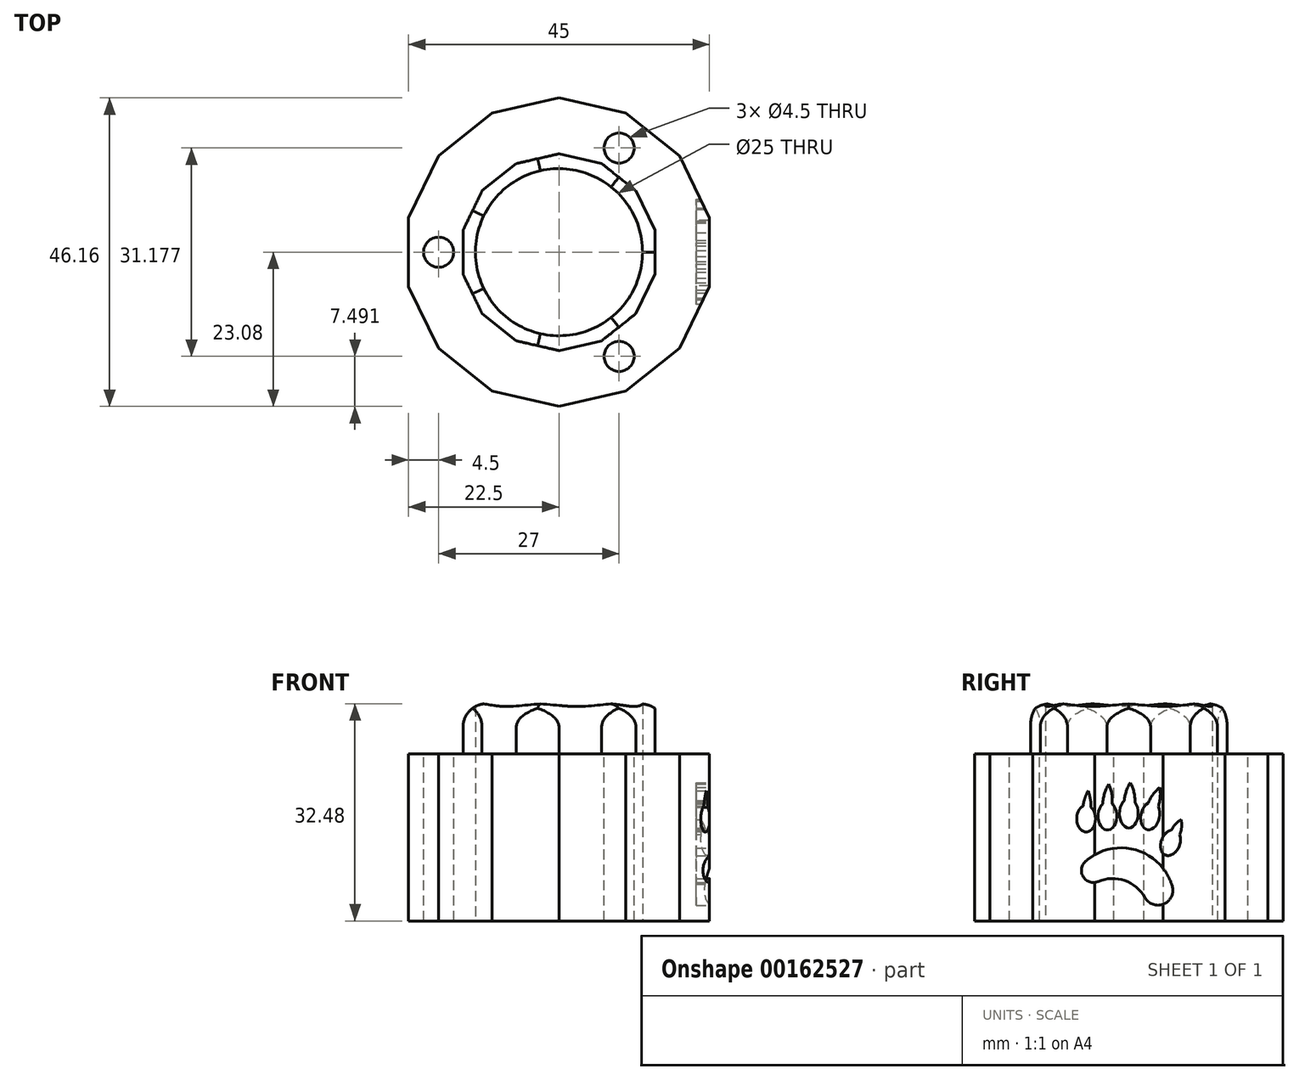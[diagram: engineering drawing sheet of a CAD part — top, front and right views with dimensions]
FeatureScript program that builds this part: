
annotation { "Feature Type Name" : "Feature", "Feature Type Description" : "" }
export const myFeature = defineFeature(function(context is Context, id is Id, definition is map)
    precondition{}
    {
        {
            var Q0;
            Q0=qCreatedBy(makeId("Top.planeOp"),FACE);
            var sketch = newSketch(context, id + "F0", { "sketchPlane" : qUnion([Q0])});
            skCircle(sketch, "E0", {"center": v(0, 0) * mm, "radius": 12.5 * mm});
            skCircle(sketch, "E1.cCircle", {"center": v(0, 0) * mm, "radius": 17.5 * mm, "construction": true});
            skLineSegment(sketch, "E1.0", {"start": v(17.5, 8.43) * mm, "end": v(17.5, -8.43) * mm, "construction": true});
            skLineSegment(sketch, "E1.1", {"start": v(17.5, -8.43) * mm, "end": v(4.32, -18.94) * mm, "construction": true});
            skLineSegment(sketch, "E1.2", {"start": v(4.32, -18.94) * mm, "end": v(-12.11, -15.19) * mm, "construction": true});
            skLineSegment(sketch, "E1.3", {"start": v(-12.11, -15.19) * mm, "end": v(-19.42, 0) * mm, "construction": true});
            skLineSegment(sketch, "E1.4", {"start": v(-19.42, 0) * mm, "end": v(-12.11, 15.19) * mm, "construction": true});
            skLineSegment(sketch, "E1.5", {"start": v(-12.11, 15.19) * mm, "end": v(4.32, 18.94) * mm, "construction": true});
            skLineSegment(sketch, "E1.6", {"start": v(4.32, 18.94) * mm, "end": v(17.5, 8.43) * mm, "construction": true});
            skPoint(sketch, "E1.0.midPoint", {"position": v(17.5, 0) * mm});
            skArc(sketch, "E2", {"start": v(7.16, 16.67) * mm, "mid": v(13.9, 17.43) * mm, "end": v(14.66, 10.69) * mm, "construction": true});
            skArc(sketch, "E3", {"start": v(0.79, 18.13) * mm, "mid": v(-4.96, 21.74) * mm, "end": v(-8.57, 16) * mm, "construction": true});
            skArc(sketch, "E4", {"start": v(-13.68, 11.92) * mm, "mid": v(-20.1, 9.68) * mm, "end": v(-17.85, 3.27) * mm, "construction": true});
            skArc(sketch, "E5", {"start": v(-17.85, -3.27) * mm, "mid": v(-20.1, -9.68) * mm, "end": v(-13.68, -11.92) * mm, "construction": true});
            skArc(sketch, "E6", {"start": v(-8.57, -16) * mm, "mid": v(-4.96, -21.74) * mm, "end": v(0.79, -18.13) * mm, "construction": true});
            skArc(sketch, "E7", {"start": v(14.66, -10.69) * mm, "mid": v(13.9, -17.43) * mm, "end": v(7.16, -16.67) * mm, "construction": true});
            skCircle(sketch, "E8.cCircle", {"center": v(0, 0) * mm, "radius": 22.5 * mm, "construction": true});
            skLineSegment(sketch, "E8.0", {"start": v(22.5, 5.14) * mm, "end": v(22.5, -5.14) * mm});
            skLineSegment(sketch, "E8.1", {"start": v(22.5, -5.14) * mm, "end": v(18.04, -14.39) * mm});
            skLineSegment(sketch, "E8.2", {"start": v(18.04, -14.39) * mm, "end": v(10.01, -20.8) * mm});
            skLineSegment(sketch, "E8.3", {"start": v(10.01, -20.8) * mm, "end": v(0, -23.08) * mm});
            skLineSegment(sketch, "E8.4", {"start": v(0, -23.08) * mm, "end": v(-10.01, -20.8) * mm});
            skLineSegment(sketch, "E8.5", {"start": v(-10.01, -20.8) * mm, "end": v(-18.04, -14.39) * mm});
            skLineSegment(sketch, "E8.6", {"start": v(-18.04, -14.39) * mm, "end": v(-22.5, -5.14) * mm});
            skLineSegment(sketch, "E8.7", {"start": v(-22.5, -5.14) * mm, "end": v(-22.5, 5.14) * mm});
            skLineSegment(sketch, "E8.8", {"start": v(-22.5, 5.14) * mm, "end": v(-18.04, 14.39) * mm});
            skLineSegment(sketch, "E8.9", {"start": v(-18.04, 14.39) * mm, "end": v(-10.01, 20.8) * mm});
            skLineSegment(sketch, "E8.10", {"start": v(-10.01, 20.8) * mm, "end": v(0, 23.08) * mm});
            skLineSegment(sketch, "E8.11", {"start": v(0, 23.08) * mm, "end": v(10.01, 20.8) * mm});
            skLineSegment(sketch, "E8.12", {"start": v(10.01, 20.8) * mm, "end": v(18.04, 14.39) * mm});
            skLineSegment(sketch, "E8.13", {"start": v(18.04, 14.39) * mm, "end": v(22.5, 5.14) * mm});
            skPoint(sketch, "E8.0.midPoint", {"position": v(22.5, 0) * mm});
            skSolve(sketch);
        }
        {
            var Q0;
            Q0=qSketchRegion(id+"F0",true);
            extrude(context, id + "F1", {"entities" : qUnion([Q0]), "endBound" : BoundingType.SYMMETRIC, "depth" : 25 * mm, "offsetDistance" : 25 * mm});
        }
        {
            var Q0;
            Q0=makeQuery(id+"F1.opExtrude","CAP_FACE",FACE,{"disambiguationData":[OSD([sQuery(id+"F0.wireOp",EDGE,"E0"),sQuery(id+"F0.wireOp",EDGE,"E1.0"),sQuery(id+"F0.wireOp",EDGE,"E1.1"),sQuery(id+"F0.wireOp",EDGE,"E1.2"),sQuery(id+"F0.wireOp",EDGE,"E1.3"),sQuery(id+"F0.wireOp",EDGE,"E1.4"),sQuery(id+"F0.wireOp",EDGE,"E1.5"),sQuery(id+"F0.wireOp",EDGE,"E1.6"),sQuery(id+"F0.wireOp",EDGE,"E2"),sQuery(id+"F0.wireOp",EDGE,"E3"),sQuery(id+"F0.wireOp",EDGE,"E4"),sQuery(id+"F0.wireOp",EDGE,"E5"),sQuery(id+"F0.wireOp",EDGE,"E6"),sQuery(id+"F0.wireOp",EDGE,"E7")])],"isStart":false});
            var sketch = newSketch(context, id + "F2", { "sketchPlane" : qUnion([Q0])});
            skLineSegment(sketch, "E9", {"start": v(0, 0) * mm, "end": v(11.38, 19.7) * mm, "construction": true});
            skCircle(sketch, "E10", {"center": v(9, 15.59) * mm, "radius": 2.25 * mm});
            skCircle(sketch, "E11.1.0", {"center": v(-18, 0) * mm, "radius": 2.25 * mm});
            skCircle(sketch, "E11.2.0", {"center": v(9, -15.59) * mm, "radius": 2.25 * mm});
            skPoint(sketch, "E11.center", {"position": v(0, 0) * mm});
            skSolve(sketch);
        }
        {
            var Q0;
            Q0=qSketchRegion(id+"F2",true);
            extrude(context, id + "F3", {"entities" : qUnion([Q0]), "operationType" : NewBodyOperationType.REMOVE, "oppositeDirection" : true, "depth" : 25 * mm, "offsetDistance" : 25 * mm});
        }
        {
            var Q0;
            Q0=makeQuery(id+"F1.opExtrude","CAP_FACE",FACE,{"disambiguationData":[OSD([sQuery(id+"F0.wireOp",EDGE,"E0"),sQuery(id+"F0.wireOp",EDGE,"E1.0"),sQuery(id+"F0.wireOp",EDGE,"E1.1"),sQuery(id+"F0.wireOp",EDGE,"E1.2"),sQuery(id+"F0.wireOp",EDGE,"E1.3"),sQuery(id+"F0.wireOp",EDGE,"E1.4"),sQuery(id+"F0.wireOp",EDGE,"E1.5"),sQuery(id+"F0.wireOp",EDGE,"E1.6"),sQuery(id+"F0.wireOp",EDGE,"E2"),sQuery(id+"F0.wireOp",EDGE,"E3"),sQuery(id+"F0.wireOp",EDGE,"E4"),sQuery(id+"F0.wireOp",EDGE,"E5"),sQuery(id+"F0.wireOp",EDGE,"E6"),sQuery(id+"F0.wireOp",EDGE,"E7")])],"isStart":false});
            var sketch = newSketch(context, id + "F4", { "sketchPlane" : qUnion([Q0])});
            skCircle(sketch, "E12", {"center": v(0, 0) * mm, "radius": 12.5 * mm});
            skCircle(sketch, "E13.cCircle", {"center": v(0, 0) * mm, "radius": 14.35 * mm, "construction": true});
            skLineSegment(sketch, "E13.0", {"start": v(14.35, 3.28) * mm, "end": v(14.35, -3.28) * mm});
            skLineSegment(sketch, "E13.1", {"start": v(14.35, -3.28) * mm, "end": v(11.5, -9.18) * mm});
            skLineSegment(sketch, "E13.2", {"start": v(11.5, -9.18) * mm, "end": v(6.39, -13.26) * mm});
            skLineSegment(sketch, "E13.3", {"start": v(6.39, -13.26) * mm, "end": v(0, -14.72) * mm});
            skLineSegment(sketch, "E13.4", {"start": v(0, -14.72) * mm, "end": v(-6.39, -13.26) * mm});
            skLineSegment(sketch, "E13.5", {"start": v(-6.39, -13.26) * mm, "end": v(-11.5, -9.18) * mm});
            skLineSegment(sketch, "E13.6", {"start": v(-11.5, -9.18) * mm, "end": v(-14.35, -3.28) * mm});
            skLineSegment(sketch, "E13.7", {"start": v(-14.35, -3.28) * mm, "end": v(-14.35, 3.28) * mm});
            skLineSegment(sketch, "E13.8", {"start": v(-14.35, 3.28) * mm, "end": v(-11.5, 9.18) * mm});
            skLineSegment(sketch, "E13.9", {"start": v(-11.5, 9.18) * mm, "end": v(-6.39, 13.26) * mm});
            skLineSegment(sketch, "E13.10", {"start": v(-6.39, 13.26) * mm, "end": v(0, 14.72) * mm});
            skLineSegment(sketch, "E13.11", {"start": v(0, 14.72) * mm, "end": v(6.39, 13.26) * mm});
            skLineSegment(sketch, "E13.12", {"start": v(6.39, 13.26) * mm, "end": v(11.5, 9.18) * mm});
            skLineSegment(sketch, "E13.13", {"start": v(11.5, 9.18) * mm, "end": v(14.35, 3.28) * mm});
            skPoint(sketch, "E13.0.midPoint", {"position": v(14.35, 0) * mm});
            skSolve(sketch);
        }
        {
            var Q0;
            Q0=qSketchRegion(id+"F4",true);
            extrude(context, id + "F5", {"entities" : qUnion([Q0]), "operationType" : NewBodyOperationType.ADD, "depth" : 7.5 * mm, "offsetDistance" : 25 * mm});
        }
        {
            var Q0;
            Q0=makeQuery(id+"F5.opExtrude","CAP_EDGE",EDGE,{"disambiguationData":[OSD([sQuery(id+"F4.wireOp",EDGE,"E13.7")])],"isStart":false});
            var Q1;
            Q1=makeQuery(id+"F5.opExtrude","CAP_EDGE",EDGE,{"disambiguationData":[OSD([sQuery(id+"F4.wireOp",EDGE,"E13.5")])],"isStart":false});
            var Q2;
            Q2=makeQuery(id+"F5.opExtrude","CAP_EDGE",EDGE,{"disambiguationData":[OSD([sQuery(id+"F4.wireOp",EDGE,"E13.3")])],"isStart":false});
            var Q3;
            Q3=makeQuery(id+"F5.opExtrude","CAP_EDGE",EDGE,{"disambiguationData":[OSD([sQuery(id+"F4.wireOp",EDGE,"E13.1")])],"isStart":false});
            var Q4;
            Q4=makeQuery(id+"F5.opExtrude","CAP_EDGE",EDGE,{"disambiguationData":[OSD([sQuery(id+"F4.wireOp",EDGE,"E13.13")])],"isStart":false});
            var Q5;
            Q5=makeQuery(id+"F5.opExtrude","CAP_EDGE",EDGE,{"disambiguationData":[OSD([sQuery(id+"F4.wireOp",EDGE,"E13.11")])],"isStart":false});
            var Q6;
            Q6=makeQuery(id+"F5.opExtrude","CAP_EDGE",EDGE,{"disambiguationData":[OSD([sQuery(id+"F4.wireOp",EDGE,"E13.9")])],"isStart":false});
            fillet(context, id + "F6", {"entities" : qUnion([Q0, Q1, Q2, Q3, Q4, Q5, Q6]), "radius" : 3.5 * mm, "tangentPropagation" : true, "allowEdgeOverflow" : false});
        }
        {
            var Q0;
            Q0=makeQuery(id+"F1.opExtrude","SWEPT_FACE",FACE,{"disambiguationData":[OSD([sQuery(id+"F0.wireOp",EDGE,"E8.0")])]});
            var sketch = newSketch(context, id + "F7", { "sketchPlane" : qUnion([Q0])});
            skEllipticalArc(sketch, "E14", {});
            skEllipticalArc(sketch, "E15", {});
            skEllipticalArc(sketch, "E16", {});
            skEllipticalArc(sketch, "E17", {});
            skEllipticalArc(sketch, "E18", {});
            skLineSegment(sketch, "E19", {"start": v(3.2, 3.2) * mm, "end": v(3.74, 5.22) * mm, "construction": true});
            skArc(sketch, "E20", {"start": v(6.4, -7) * mm, "mid": v(0.86, -1.84) * mm, "end": v(-6.5, -3.6) * mm});
            skArc(sketch, "E21", {"start": v(-6.5, -3.6) * mm, "mid": v(-6.82, -5.9) * mm, "end": v(-4.6, -6.6) * mm});
            skArc(sketch, "E22", {"start": v(2.4, -9) * mm, "mid": v(-0.64, -6.46) * mm, "end": v(-4.6, -6.6) * mm});
            skArc(sketch, "E23", {"start": v(2.4, -9) * mm, "mid": v(5.35, -9.9) * mm, "end": v(6.4, -7) * mm});
            skArc(sketch, "E24", {"start": v(-6.08, 7) * mm, "mid": v(-6.57, 5.88) * mm, "end": v(-6.84, 4.7) * mm});
            skArc(sketch, "E25", {"start": v(-5.64, 4.48) * mm, "mid": v(-5.76, 5.76) * mm, "end": v(-6.08, 7) * mm});
            skArc(sketch, "E26", {"start": v(-3, 8) * mm, "mid": v(-3.63, 6.56) * mm, "end": v(-3.9, 5.02) * mm});
            skArc(sketch, "E27", {"start": v(-2.5, 5.02) * mm, "mid": v(-2.56, 6.54) * mm, "end": v(-3, 8) * mm});
            skArc(sketch, "E28", {"start": v(0.23, 8.2) * mm, "mid": v(-0.38, 6.92) * mm, "end": v(-0.67, 5.53) * mm});
            skArc(sketch, "E29", {"start": v(0.93, 5.25) * mm, "mid": v(0.77, 6.77) * mm, "end": v(0.23, 8.2) * mm});
            skArc(sketch, "E30", {"start": v(4.63, 7.5) * mm, "mid": v(3.61, 6.42) * mm, "end": v(2.9, 5.13) * mm});
            skArc(sketch, "E31", {"start": v(4.4, 4.6) * mm, "mid": v(4.7, 6.04) * mm, "end": v(4.63, 7.5) * mm});
            skArc(sketch, "E32", {"start": v(7.83, 2.64) * mm, "mid": v(6.98, 1.99) * mm, "end": v(6.39, 1.1) * mm});
            skArc(sketch, "E33", {"start": v(7.61, 0.4) * mm, "mid": v(7.9, 1.5) * mm, "end": v(7.83, 2.64) * mm});
            const initialGuessF7  = {"E14": [-0.0064, 0.0028, 0, -1, 0.002, 0.0014, 3.4647722976741355, 2.5716786325311984], "E15": [-0.0032, 0.0032, 0, -1, 0.0021, 0.0014, 3.6651914291880905, 2.617993877991494], "E16": [0, 0.0036, 0, -1, 0.0022, 0.0014, 3.6426090526539325, 2.417388051673486], "E17": [0.0032, 0.0032, -0.2012802899150022, -0.9795336874716115, 0.0021, 0.0014, 3.6564949123168993, 2.4469535074293285], "E18": [0.0062397368307141226, -0.0008, -0.38482758259633654, -0.9229884786242242, 0.002, 0.0014, 3.5803471543548775, 2.5286516265661505]};
            skSetInitialGuess(sketch, initialGuessF7);
            skSolve(sketch);
        }
        {
            var Q0;
            Q0=qSketchRegion(id+"F7",true);
            extrude(context, id + "F8", {"entities" : qUnion([Q0]), "operationType" : NewBodyOperationType.REMOVE, "oppositeDirection" : true, "depth" : 2 * mm, "offsetDistance" : 25 * mm});
        }
    });
